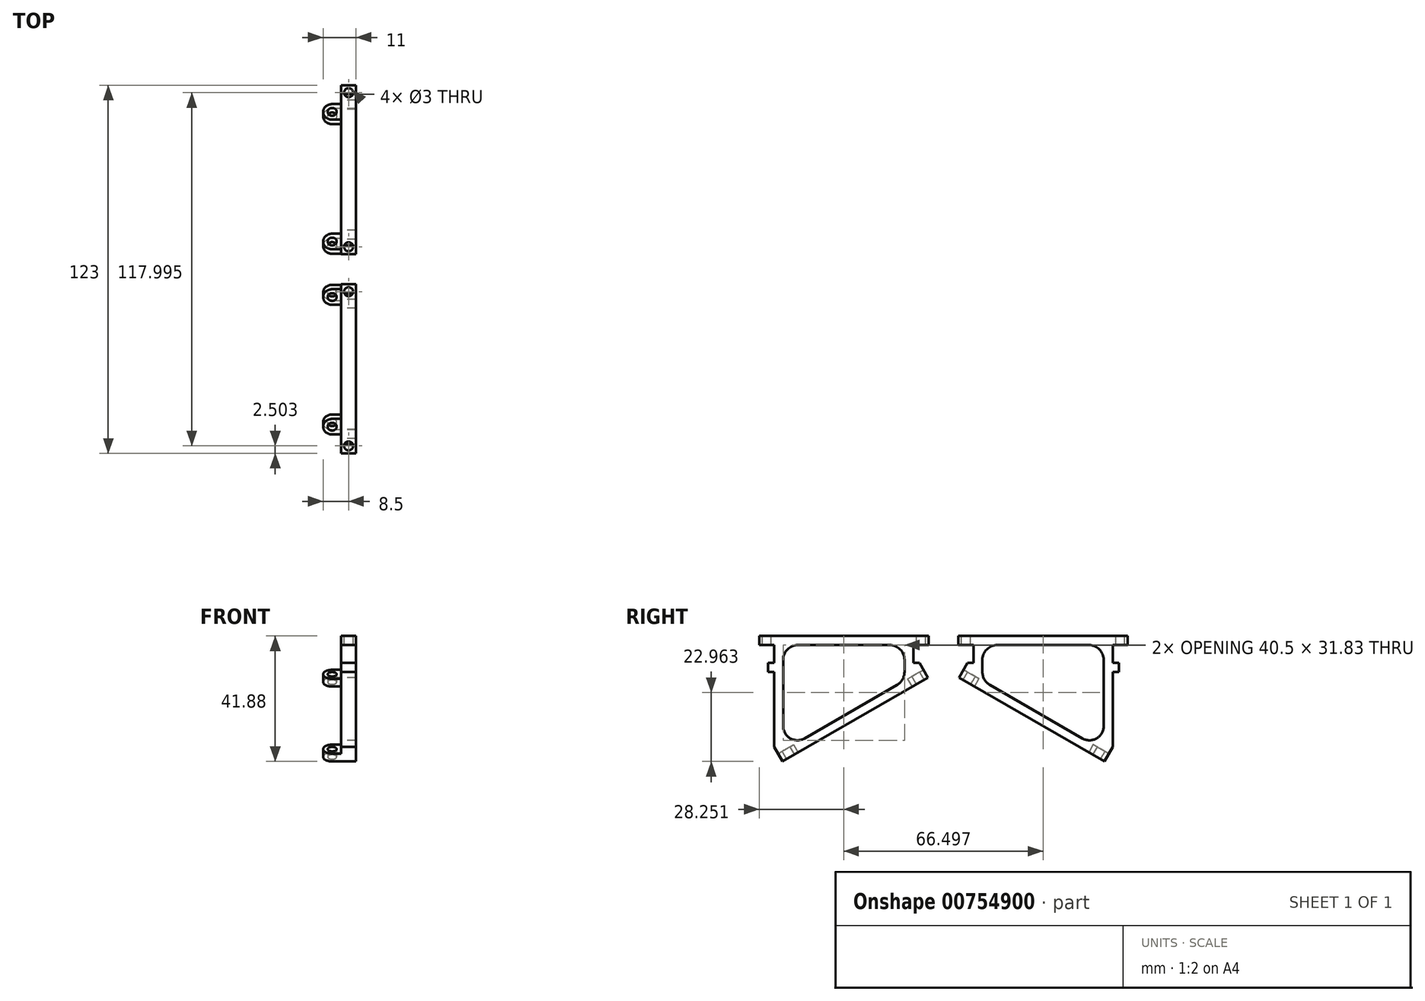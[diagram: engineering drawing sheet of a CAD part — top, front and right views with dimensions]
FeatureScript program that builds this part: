
annotation { "Feature Type Name" : "Feature", "Feature Type Description" : "" }
export const myFeature = defineFeature(function(context is Context, id is Id, definition is map)
    precondition{}
    {
        {
            var Q0;
            Q0=qCreatedBy(makeId("Right.planeOp"),FACE);
            var sketch = newSketch(context, id + "F0", { "sketchPlane" : qUnion([Q0])});
            skLineSegment(sketch, "E0.bottom", {"start": v(0, 0) * mm, "end": v(15, 0) * mm});
            skLineSegment(sketch, "E0.left", {"start": v(0, 0) * mm, "end": v(0, -3) * mm});
            skLineSegment(sketch, "E1.bottom", {"start": v(0, -3) * mm, "end": v(5, -3) * mm});
            skLineSegment(sketch, "E1.top", {"start": v(3, -9) * mm, "end": v(5, -9) * mm});
            skLineSegment(sketch, "E1.right", {"start": v(5, -3) * mm, "end": v(5, -9) * mm});
            skLineSegment(sketch, "E2", {"start": v(0.18, -13.88) * mm, "end": v(48.68, -41.88) * mm});
            skLineSegment(sketch, "E3", {"start": v(48.68, -41.88) * mm, "end": v(51.5, -37) * mm});
            skLineSegment(sketch, "E4", {"start": v(41.36, -34.2) * mm, "end": v(10.5, -16.38) * mm});
            skLineSegment(sketch, "E5.bottom", {"start": v(56.5, 0) * mm, "end": v(48.5, 0) * mm});
            skLineSegment(sketch, "E5.top", {"start": v(53.5, -12) * mm, "end": v(51.5, -12) * mm});
            skLineSegment(sketch, "E5.left", {"start": v(56.5, 0) * mm, "end": v(56.5, -3) * mm});
            skLineSegment(sketch, "E5.right", {"start": v(48.5, -8) * mm, "end": v(48.5, -12) * mm});
            skLineSegment(sketch, "E6.bottom", {"start": v(56.5, -3) * mm, "end": v(51.5, -3) * mm});
            skLineSegment(sketch, "E6.top", {"start": v(53.5, -9) * mm, "end": v(51.5, -9) * mm});
            skLineSegment(sketch, "E6.right", {"start": v(51.5, -3) * mm, "end": v(51.5, -9) * mm});
            skLineSegment(sketch, "E7.bottom", {"start": v(51.5, -37) * mm, "end": v(51.5, -37) * mm});
            skLineSegment(sketch, "E7.top", {"start": v(51.5, -12) * mm, "end": v(51.5, -12) * mm});
            skLineSegment(sketch, "E7.right", {"start": v(51.5, -37) * mm, "end": v(51.5, -12) * mm});
            skLineSegment(sketch, "E8.bottom", {"start": v(48.5, -12) * mm, "end": v(48.5, -12) * mm});
            skLineSegment(sketch, "E8.top", {"start": v(48.5, -38.32) * mm, "end": v(48.5, -38.32) * mm});
            skLineSegment(sketch, "E8.left", {"start": v(48.5, -12) * mm, "end": v(48.5, -30.07) * mm});
            skLineSegment(sketch, "E8.right", {"start": v(48.5, -12) * mm, "end": v(48.5, -30.07) * mm});
            skLineSegment(sketch, "E9.trimOffspring", {"start": v(53.5, -9) * mm, "end": v(53.5, -12) * mm});
            skLineSegment(sketch, "E10.bottom", {"start": v(15, 0) * mm, "end": v(48.5, 0) * mm});
            skLineSegment(sketch, "E10.top", {"start": v(20, -3) * mm, "end": v(43.5, -3) * mm});
            skPoint(sketch, "E11.visualSharp", {"position": v(6.94, -3) * mm});
            skPoint(sketch, "E12.visualSharp", {"position": v(8.26, -15.09) * mm});
            skPoint(sketch, "E13.visualSharp", {"position": v(48.5, -3) * mm});
            skArc(sketch, "E13.filletArc", {"start": v(48.5, -8) * mm, "mid": v(47.03, -4.46) * mm, "end": v(43.5, -3) * mm});
            skPoint(sketch, "E14.visualSharp", {"position": v(48.5, -38.32) * mm});
            skArc(sketch, "E14.filletArc", {"start": v(41.36, -34.2) * mm, "mid": v(46.12, -34.2) * mm, "end": v(48.5, -30.07) * mm});
            skPoint(sketch, "E0.right.start.orphan", {"position": v(15, -10) * mm});
            skLineSegment(sketch, "E15", {"start": v(20, -3) * mm, "end": v(13, -3) * mm});
            skLineSegment(sketch, "E16", {"start": v(0.18, -13.88) * mm, "end": v(3, -9) * mm});
            skPoint(sketch, "E17.trimOffspring.start.orphan", {"position": v(-0.89, -9) * mm});
            skPoint(sketch, "E18.filletArc.end.orphan", {"position": v(10, -10) * mm});
            skLineSegment(sketch, "E19", {"start": v(8, -8) * mm, "end": v(8, -12.05) * mm});
            skPoint(sketch, "E20.visualSharp", {"position": v(8, -3) * mm});
            skArc(sketch, "E20.filletArc", {"start": v(13, -3) * mm, "mid": v(9.46, -4.46) * mm, "end": v(8, -8) * mm});
            skPoint(sketch, "E21.visualSharp", {"position": v(8, -14.94) * mm});
            skArc(sketch, "E21.filletArc", {"start": v(8, -12.05) * mm, "mid": v(8.67, -14.55) * mm, "end": v(10.5, -16.38) * mm});
            skSolve(sketch);
        }
        {
            var Q0;
            Q0=makeQuery(id+"F0.imprint","IMPRINT",FACE,{"disambiguationData":[TD([[makeQuery(id+"F0.imprint","IMPRINT",EDGE,{"derivedFrom":sQuery(id+"F0.wireOp",EDGE,"E0.bottom")}),-1.0]])]});
            extrude(context, id + "F1", {"entities" : qUnion([Q0]), "depth" : 5 * mm, "offsetDistance" : 25 * mm});
        }
        {
            var Q0;
            Q0=makeQuery(id+"F1.opExtrude","CAP_FACE",FACE,{"disambiguationData":[OSD([sQuery(id+"F0.wireOp",EDGE,"E0.bottom"),sQuery(id+"F0.wireOp",EDGE,"E0.left"),sQuery(id+"F0.wireOp",EDGE,"E0.right"),sQuery(id+"F0.wireOp",EDGE,"E1.bottom"),sQuery(id+"F0.wireOp",EDGE,"E1.top"),sQuery(id+"F0.wireOp",EDGE,"E1.right"),sQuery(id+"F0.wireOp",EDGE,"E2"),sQuery(id+"F0.wireOp",EDGE,"E3"),sQuery(id+"F0.wireOp",EDGE,"E4"),sQuery(id+"F0.wireOp",EDGE,"E5.bottom"),sQuery(id+"F0.wireOp",EDGE,"E5.top"),sQuery(id+"F0.wireOp",EDGE,"E5.left"),sQuery(id+"F0.wireOp",EDGE,"E5.right"),sQuery(id+"F0.wireOp",EDGE,"E6.bottom"),sQuery(id+"F0.wireOp",EDGE,"E6.top"),sQuery(id+"F0.wireOp",EDGE,"E6.right"),sQuery(id+"F0.wireOp",EDGE,"E7.right"),sQuery(id+"F0.wireOp",EDGE,"E8.right"),sQuery(id+"F0.wireOp",EDGE,"E9.trimOffspring"),sQuery(id+"F0.wireOp",EDGE,"E17.trimOffspring"),sQuery(id+"F0.wireOp",EDGE,"E10.bottom"),sQuery(id+"F0.wireOp",EDGE,"E10.top"),sQuery(id+"F0.wireOp",EDGE,"E11.filletArc"),sQuery(id+"F0.wireOp",EDGE,"E12.filletArc"),sQuery(id+"F0.wireOp",EDGE,"E13.filletArc"),sQuery(id+"F0.wireOp",EDGE,"E14.filletArc")])],"isStart":true});
            var sketch = newSketch(context, id + "F2", { "sketchPlane" : qUnion([Q0])});
            skLineSegment(sketch, "E22", {"start": v(-48.68, -41.88) * mm, "end": v(-43.48, -38.88) * mm});
            skLineSegment(sketch, "E23", {"start": v(-0.18, -13.88) * mm, "end": v(-5.38, -16.88) * mm});
            skLineSegment(sketch, "E24", {"start": v(-5.38, -16.88) * mm, "end": v(-6.88, -14.29) * mm});
            skLineSegment(sketch, "E25", {"start": v(-6.88, -14.29) * mm, "end": v(-1.68, -11.29) * mm});
            skLineSegment(sketch, "E26", {"start": v(-1.68, -11.29) * mm, "end": v(-0.18, -13.88) * mm});
            skLineSegment(sketch, "E27", {"start": v(-50.18, -39.29) * mm, "end": v(-44.98, -36.29) * mm});
            skLineSegment(sketch, "E28", {"start": v(-44.98, -36.29) * mm, "end": v(-43.48, -38.88) * mm});
            skPoint(sketch, "E29.orphan", {"position": v(-50.09, -39.44) * mm});
            skPoint(sketch, "E30.start.orphan", {"position": v(-47.24, -42.83) * mm});
            skLineSegment(sketch, "E31", {"start": v(-48.68, -41.88) * mm, "end": v(-50.18, -39.29) * mm});
            skSolve(sketch);
        }
        {
            var Q0;
            Q0=makeQuery(id+"F2.imprint","IMPRINT",FACE,{"disambiguationData":[TD([[makeQuery(id+"F2.imprint","IMPRINT",EDGE,{"derivedFrom":sQuery(id+"F2.wireOp",EDGE,"E23")}),-1.0]])]});
            var Q1;
            Q1=makeQuery(id+"F2.imprint","IMPRINT",FACE,{"disambiguationData":[TD([[makeQuery(id+"F2.imprint","IMPRINT",EDGE,{"derivedFrom":sQuery(id+"F2.wireOp",EDGE,"E22")}),-1.0]])]});
            extrude(context, id + "F3", {"entities" : qUnion([Q0, Q1]), "operationType" : NewBodyOperationType.ADD, "depth" : 6 * mm, "offsetDistance" : 25 * mm});
        }
        {
            var Q0;
            Q0=makeQuery(id+"F1.opExtrude","SWEPT_FACE",FACE,{"disambiguationData":[OSD([sQuery(id+"F0.wireOp",EDGE,"E0.bottom"),sQuery(id+"F0.wireOp",EDGE,"E5.bottom"),sQuery(id+"F0.wireOp",EDGE,"E10.bottom")])]});
            var sketch = newSketch(context, id + "F4", { "sketchPlane" : qUnion([Q0])});
            skCircle(sketch, "E32", {"center": v(2.5, 54) * mm, "radius": 1.5 * mm});
            skCircle(sketch, "E33", {"center": v(2.5, 2.5) * mm, "radius": 1.5 * mm});
            skSolve(sketch);
        }
        {
            var Q0;
            Q0=makeQuery(id+"F4.imprint","IMPRINT",FACE,{"disambiguationData":[TD([[makeQuery(id+"F4.imprint","IMPRINT",EDGE,{"derivedFrom":sQuery(id+"F4.wireOp",EDGE,"E33")}),1.0]])]});
            var Q1;
            Q1=makeQuery(id+"F4.imprint","IMPRINT",FACE,{"disambiguationData":[TD([[makeQuery(id+"F4.imprint","IMPRINT",EDGE,{"derivedFrom":sQuery(id+"F4.wireOp",EDGE,"E32")}),1.0]])]});
            extrude(context, id + "F5", {"entities" : qUnion([Q0, Q1]), "operationType" : NewBodyOperationType.REMOVE, "endBound" : BoundingType.UP_TO_NEXT, "oppositeDirection" : true, "depth" : 25 * mm, "offsetDistance" : 25 * mm});
        }
        {
            var Q0;
            Q0=makeQuery(id+"F3.boolean.opBoolean","MERGE",FACE,{"derivedFrom":[makeQuery(id+"F1.opExtrude","SWEPT_FACE",FACE,{"disambiguationData":[OSD([sQuery(id+"F0.wireOp",EDGE,"E2")])]}),makeQuery(id+"F3.opExtrude","SWEPT_FACE",FACE,{"disambiguationData":[OSD([sQuery(id+"F2.wireOp",EDGE,"E22")])]}),makeQuery(id+"F3.opExtrude","SWEPT_FACE",FACE,{"disambiguationData":[OSD([sQuery(id+"F2.wireOp",EDGE,"E23")])]})]});
            var sketch = newSketch(context, id + "F6", { "sketchPlane" : qUnion([Q0])});
            skCircle(sketch, "E34", {"center": v(-3, -10.1) * mm, "radius": 1.5 * mm});
            skCircle(sketch, "E35", {"center": v(-3, -60.1) * mm, "radius": 1.5 * mm});
            skSolve(sketch);
        }
        {
            var Q0;
            Q0 = qSketchRegion(id + "F6", true);
            extrude(context, id + "F7", {"entities" : qUnion([Q0]), "operationType" : NewBodyOperationType.REMOVE, "oppositeDirection" : true, "depth" : 25 * mm, "offsetDistance" : 25 * mm});
        }
        {
            var Q0;
            Q0=makeQuery(id+"F3.opExtrude","CAP_EDGE",EDGE,{"disambiguationData":[OSD([sQuery(id+"F2.wireOp",EDGE,"E26")])],"isStart":false});
            var Q1;
            Q1=makeQuery(id+"F3.opExtrude","CAP_EDGE",EDGE,{"disambiguationData":[OSD([sQuery(id+"F2.wireOp",EDGE,"E24")])],"isStart":false});
            var Q2;
            Q2=makeQuery(id+"F3.opExtrude","CAP_EDGE",EDGE,{"disambiguationData":[OSD([sQuery(id+"F2.wireOp",EDGE,"E28")])],"isStart":false});
            var Q3;
            Q3=makeQuery(id+"F3.opExtrude","CAP_EDGE",EDGE,{"disambiguationData":[OSD([sQuery(id+"F2.wireOp",EDGE,"E31")])],"isStart":false});
            fillet(context, id + "F8", {"entities" : qUnion([Q0, Q1, Q2, Q3]), "radius" : 3 * mm, "tangentPropagation" : true, "allowEdgeOverflow" : false});
        }
        {
            var Q0;
            Q0=qCreatedBy(makeId("Front.planeOp"),FACE);
            cPlane(context, id + "F9", {"entities" : qUnion([Q0]), "cplaneType" : CPlaneType.OFFSET, "offset" : 5 * mm, "width" : 150 * mm, "height" : 150 * mm});
        }
        {
            var Q0;
            Q0=makeQuery(id+"F1.opExtrude","SWEPT_BODY",BODY,{"disambiguationData":[OSD([sQuery(id+"F0.wireOp",EDGE,"E0.bottom"),sQuery(id+"F0.wireOp",EDGE,"E0.left"),sQuery(id+"F0.wireOp",EDGE,"E1.bottom"),sQuery(id+"F0.wireOp",EDGE,"E1.top"),sQuery(id+"F0.wireOp",EDGE,"E1.right"),sQuery(id+"F0.wireOp",EDGE,"E2"),sQuery(id+"F0.wireOp",EDGE,"E3"),sQuery(id+"F0.wireOp",EDGE,"E4"),sQuery(id+"F0.wireOp",EDGE,"E5.bottom"),sQuery(id+"F0.wireOp",EDGE,"E5.top"),sQuery(id+"F0.wireOp",EDGE,"E5.left"),sQuery(id+"F0.wireOp",EDGE,"E5.right"),sQuery(id+"F0.wireOp",EDGE,"E6.bottom"),sQuery(id+"F0.wireOp",EDGE,"E6.top"),sQuery(id+"F0.wireOp",EDGE,"E6.right"),sQuery(id+"F0.wireOp",EDGE,"E7.right"),sQuery(id+"F0.wireOp",EDGE,"E8.right"),sQuery(id+"F0.wireOp",EDGE,"E9.trimOffspring"),sQuery(id+"F0.wireOp",EDGE,"E10.bottom"),sQuery(id+"F0.wireOp",EDGE,"E10.top"),sQuery(id+"F0.wireOp",EDGE,"E13.filletArc"),sQuery(id+"F0.wireOp",EDGE,"E14.filletArc"),sQuery(id+"F0.wireOp",EDGE,"E15"),sQuery(id+"F0.wireOp",EDGE,"E16"),sQuery(id+"F0.wireOp",EDGE,"E19"),sQuery(id+"F0.wireOp",EDGE,"E20.filletArc"),sQuery(id+"F0.wireOp",EDGE,"E21.filletArc")])]});
            var Q1;
            Q1=qCreatedBy(id+"F9.planeOp",FACE);
            mirror(context, id + "F10", {"entities" : qUnion([Q0]), "mirrorPlane" : qUnion([Q1])});
        }
    });
